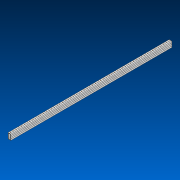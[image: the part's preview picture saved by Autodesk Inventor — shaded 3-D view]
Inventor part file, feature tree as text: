
AUTODESK INVENTOR PART (.ipt)
format: ipt  version: 2022.2 (Build 262287000, 287)  size: 586,240 bytes
history: native  units: in
note: dims shown in document units (in); Inventor stores cm internally (conversion verified against a paired STEP export)
features: other x60, extrude x1, pattern_linear x1, sketch x1
ambient origin geometry x8: Origin, YZ Plane, XZ Plane, XY Plane, X Axis, Y Axis, Z Axis, Center Point
bodies: Solid1 (feature_tree)
feature tree (63):
  extrude  "Extrusion1"  Depth=2.0in
  other  "Work Axis1"
  pattern_linear  "Rectangular Pattern1"  Spacing1=0.0in  [1 undecoded]
  sketch  "Sketch1"  dims[d0=1.0in d1=2.0in d2=0.0in d3=0.0in d4=23.2283in d6=1.0in]
  other  "Work Axis2"
  other  "Work Axis3"
  other  "Work Axis4"
  other  "Work Axis5"
  other  "Work Axis6"
  other  "Work Axis7"
  other  "Work Axis8"
  other  "Work Axis9"
  other  "Work Axis10"
  other  "Work Axis11"
  other  "Work Axis12"
  other  "Work Axis13"
  other  "Work Axis14"
  other  "Work Axis15"
  other  "Work Axis16"
  other  "Work Axis17"
  other  "Work Axis18"
  other  "Work Axis19"
  other  "Work Axis20"
  other  "Work Axis21"
  other  "Work Axis22"
  other  "Work Axis23"
  other  "Work Axis24"
  other  "Work Axis25"
  other  "Work Axis26"
  other  "Work Axis27"
  other  "Work Axis28"
  other  "Work Axis29"
  other  "Work Axis30"
  other  "Work Axis31"
  other  "Work Axis32"
  other  "Work Axis33"
  other  "Work Axis34"
  other  "Work Axis35"
  other  "Work Axis36"
  other  "Work Axis37"
  other  "Work Axis38"
  other  "Work Axis39"
  other  "Work Axis40"
  other  "Work Axis41"
  other  "Work Axis42"
  other  "Work Axis43"
  other  "Work Axis44"
  other  "Work Axis45"
  other  "Work Axis46"
  other  "Work Axis47"
  other  "Work Axis48"
  other  "Work Axis49"
  other  "Work Axis50"
  other  "Work Axis51"
  other  "Work Axis52"
  other  "Work Axis53"
  other  "Work Axis54"
  other  "Work Axis55"
  other  "Work Axis56"
  other  "Work Axis57"
  other  "Work Axis58"
  other  "Work Axis59"
  other  "Cut-Extrude2"
note: 1 required parameter value undecoded (feature->parameter linkage not recoverable at this tier; creation-order binding heuristic only, values carry confidence <= 0.55)
